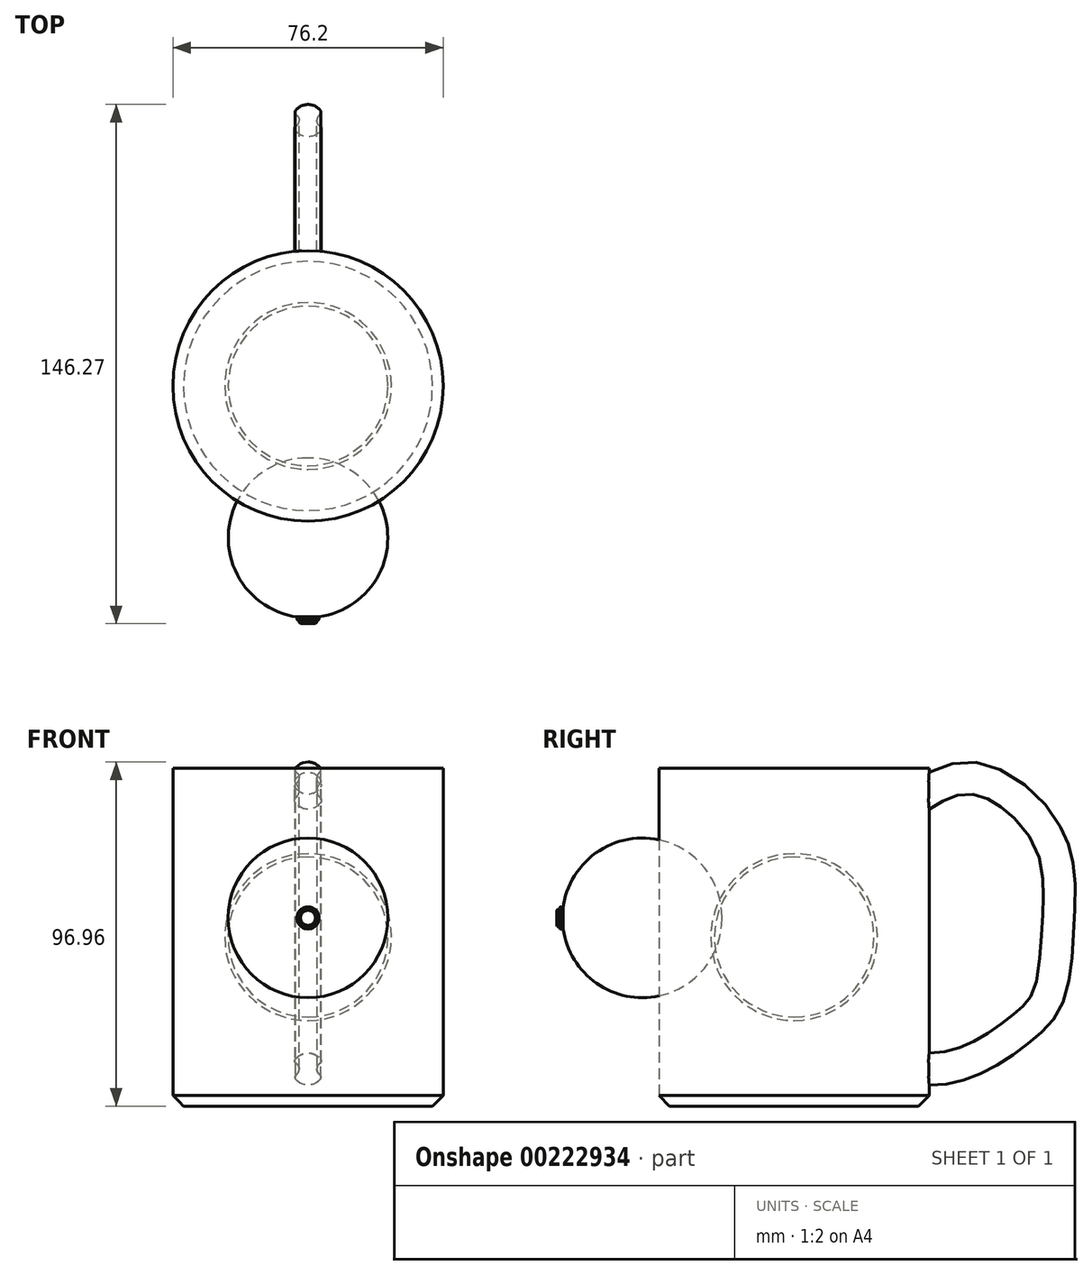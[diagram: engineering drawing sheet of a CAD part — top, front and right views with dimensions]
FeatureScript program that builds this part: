
annotation { "Feature Type Name" : "Feature", "Feature Type Description" : "" }
export const myFeature = defineFeature(function(context is Context, id is Id, definition is map)
    precondition{}
    {
        {
            var Q0;
            Q0=qCreatedBy(makeId("Front.planeOp"),FACE);
            var sketch = newSketch(context, id + "F0", { "sketchPlane" : qUnion([Q0])});
            skLineSegment(sketch, "E0.bottom", {"start": v(0, 0) * mm, "end": v(38.1, 0) * mm});
            skLineSegment(sketch, "E0.top", {"start": v(0, 95.25) * mm, "end": v(38.1, 95.25) * mm});
            skLineSegment(sketch, "E0.left", {"start": v(0, 0) * mm, "end": v(0, 95.25) * mm});
            skLineSegment(sketch, "E0.right", {"start": v(38.1, 0) * mm, "end": v(38.1, 95.25) * mm});
            skSolve(sketch);
        }
        {
            var Q0;
            Q0=makeQuery(id+"F0.imprint","IMPRINT",FACE,{"disambiguationData":[TD([[makeQuery(id+"F0.imprint","IMPRINT",EDGE,{"derivedFrom":sQuery(id+"F0.wireOp",EDGE,"E0.bottom")}),1.0]])]});
            var Q1;
            Q1=sQuery(id+"F0.wireOp",EDGE,"E0.left");
            revolve(context, id + "F1", {"entities" : qUnion([Q0]), "axis" : qUnion([Q1]), "revolveType" : RevolveType.FULL});
        }
        {
            var Q0;
            Q0=makeQuery(id+"F1.opRevolve","SWEPT_FACE",FACE,{"disambiguationData":[OSD([sQuery(id+"F0.wireOp",EDGE,"E0.top")])]});
            var Q1;
            Q1=makeQuery(id+"F1.opRevolve","SWEPT_FACE",FACE,{"disambiguationData":[OSD([sQuery(id+"F0.wireOp",EDGE,"E0.bottom")])]});
            cPlane(context, id + "F2", {"entities" : qUnion([Q0, Q1]), "cplaneType" : CPlaneType.MID_PLANE, "offset" : 25 * mm, "width" : 150 * mm, "height" : 150 * mm});
        }
        {
            var Q0;
            Q0=qCreatedBy(id+"F2.planeOp",FACE);
            var sketch = newSketch(context, id + "F3", { "sketchPlane" : qUnion([Q0])});
            skArc(sketch, "E1", {"start": v(0, -22.5) * mm, "mid": v(22.5, 0) * mm, "end": v(0, 22.5) * mm});
            skArc(sketch, "E2.0", {"start": v(0, -23.5) * mm, "mid": v(23.5, 0) * mm, "end": v(0, 23.5) * mm});
            skLineSegment(sketch, "E3", {"start": v(0, -29.7) * mm, "end": v(0, 30.26) * mm});
            skLineSegment(sketch, "E4.bottom", {"start": v(0, -23.95) * mm, "end": v(4, -23.95) * mm});
            skLineSegment(sketch, "E4.top", {"start": v(0, -22.14) * mm, "end": v(4, -22.14) * mm});
            skLineSegment(sketch, "E4.left", {"start": v(0, -23.95) * mm, "end": v(0, -22.14) * mm});
            skLineSegment(sketch, "E4.right", {"start": v(4, -23.95) * mm, "end": v(4, -22.14) * mm});
            skLineSegment(sketch, "E5.bottom", {"start": v(0, -24.95) * mm, "end": v(2, -24.95) * mm});
            skLineSegment(sketch, "E5.top", {"start": v(0, -22.41) * mm, "end": v(2, -22.41) * mm});
            skLineSegment(sketch, "E5.left", {"start": v(0, -24.95) * mm, "end": v(0, -22.41) * mm});
            skLineSegment(sketch, "E5.right", {"start": v(2, -24.95) * mm, "end": v(2, -23.95) * mm});
            skLineSegment(sketch, "E6", {"start": v(2, -23.95) * mm, "end": v(2, -22.41) * mm});
            skSolve(sketch);
        }
        {
            var Q0;
            {var subQ0=sQuery(id+"F3.wireOp",EDGE,"E1");Q0=makeQuery(id+"F3.imprint","IMPRINT",FACE,{"disambiguationData":[TD([[makeQuery(id+"F3.imprint","IMPRINT",EDGE,{"derivedFrom":subQ0}),1.0]])]});}
            var Q1;
            {var subQ0=sQuery(id+"F3.wireOp",EDGE,"E4.top");Q1=makeQuery(id+"F3.imprint","IMPRINT",FACE,{"disambiguationData":[TD([[makeQuery(id+"F3.imprint","IMPRINT",EDGE,{"derivedFrom":subQ0}),-1.0]])]});}
            var Q2;
            Q2=sQuery(id+"F3.wireOp",EDGE,"E3");
            revolve(context, id + "F4", {"entities" : qUnion([Q0, Q1]), "axis" : qUnion([Q2]), "revolveType" : RevolveType.FULL});
        }
        {
            var Q0;
            {var subQ0=sQuery(id+"F3.wireOp",EDGE,"E1");Q0=makeQuery(id+"F3.imprint","IMPRINT",FACE,{"disambiguationData":[TD([[makeQuery(id+"F3.imprint","IMPRINT",EDGE,{"derivedFrom":subQ0}),-1.0]])]});}
            var Q1;
            Q1=sQuery(id+"F3.wireOp",EDGE,"E3");
            revolve(context, id + "F5", {"entities" : qUnion([Q0]), "axis" : qUnion([Q1]), "revolveType" : RevolveType.FULL});
        }
        {
            var Q0;
            Q0=qCreatedBy(makeId("Front.planeOp"),FACE);
            var sketch = newSketch(context, id + "F6", { "sketchPlane" : qUnion([Q0])});
            skCircle(sketch, "E7", {"center": v(0, 47.62) * mm, "radius": 22.5 * mm});
            skCircle(sketch, "E8", {"center": v(0, 47.62) * mm, "radius": 23.5 * mm});
            skLineSegment(sketch, "E9", {"start": v(0, 47.62) * mm, "end": v(22.5, 47.62) * mm, "construction": true});
            skLineSegment(sketch, "E10", {"start": v(0, 47.62) * mm, "end": v(22.42, 49.54) * mm, "construction": true});
            skLineSegment(sketch, "E11", {"start": v(22.42, 49.54) * mm, "end": v(23.41, 49.62) * mm});
            skLineSegment(sketch, "E12", {"start": v(23.41, 49.62) * mm, "end": v(28.14, 50.03) * mm, "construction": true});
            skLineSegment(sketch, "E13", {"start": v(23.5, 47.62) * mm, "end": v(28.14, 47.62) * mm, "construction": true});
            skLineSegment(sketch, "E14", {"start": v(22.5, 47.62) * mm, "end": v(23.5, 47.62) * mm});
            skLineSegment(sketch, "E15.MirrorCS", {"start": v(22.42, 45.71) * mm, "end": v(23.41, 45.63) * mm});
            skLineSegment(sketch, "E16", {"start": v(0, 47.62) * mm, "end": v(0, 68.38) * mm, "construction": true});
            skSolve(sketch);
        }
        {
            var Q0;
            {var subQ0=sQuery(id+"F6.wireOp",EDGE,"E11");Q0=makeQuery(id+"F6.imprint","IMPRINT",FACE,{"disambiguationData":[TD([[makeQuery(id+"F6.imprint","IMPRINT",EDGE,{"derivedFrom":subQ0}),-1.0]])]});}
            var Q1;
            {var subQ0=sQuery(id+"F6.wireOp",EDGE,"E14");Q1=makeQuery(id+"F6.imprint","IMPRINT",FACE,{"disambiguationData":[TD([[makeQuery(id+"F6.imprint","IMPRINT",EDGE,{"derivedFrom":subQ0}),-1.0]])]});}
            var Q2;
            Q2=sQuery(id+"F6.wireOp",EDGE,"E16");
            revolve(context, id + "F7", {"operationType" : NewBodyOperationType.REMOVE, "entities" : qUnion([Q0, Q1]), "axis" : qUnion([Q2]), "revolveType" : RevolveType.FULL, "oppositeDirection" : true});
        }
        {
            var Q0;
            {var subQ0=sQuery(id+"F3.wireOp",EDGE,"E5.left");var subQ5=sQuery(id+"F3.wireOp",EDGE,"E2.0");var subQ6=makeQuery(id+"F3.imprint","INTERSECT",VERTEX,{"derivedFrom":[subQ5,subQ0]});Q0=makeQuery(id+"F3.imprint","IMPRINT",FACE,{"disambiguationData":[TD([[makeQuery(id+"F3.imprint","IMPRINT",EDGE,{"disambiguationData":[TD([[subQ6,-1.0]])],"derivedFrom":subQ5}),1.0]])]});}
            var Q1;
            {var subQ0=sQuery(id+"F3.wireOp",EDGE,"E4.right");var subQ5=sQuery(id+"F3.wireOp",EDGE,"E2.0");var subQ6=makeQuery(id+"F3.imprint","INTERSECT",VERTEX,{"derivedFrom":[subQ5,subQ0]});Q1=makeQuery(id+"F3.imprint","IMPRINT",FACE,{"disambiguationData":[TD([[makeQuery(id+"F3.imprint","IMPRINT",EDGE,{"disambiguationData":[TD([[subQ6,1.0]])],"derivedFrom":subQ5}),1.0]])]});}
            var Q2;
            Q2=sQuery(id+"F3.wireOp",EDGE,"E4.left");
            revolve(context, id + "F8", {"operationType" : NewBodyOperationType.REMOVE, "entities" : qUnion([Q0, Q1]), "axis" : qUnion([Q2]), "revolveType" : RevolveType.FULL, "oppositeDirection" : true});
        }
        {
            var Q0;
            Q0=qCreatedBy(id+"F2.planeOp",FACE);
            var sketch = newSketch(context, id + "F9", { "sketchPlane" : qUnion([Q0])});
            skArc(sketch, "E17.0.0", {"start": v(3.47, -23.16) * mm, "mid": v(0, 23.41) * mm, "end": v(-3.47, -23.16) * mm, "construction": true});
            skLineSegment(sketch, "E17.0.1", {"start": v(-3.47, -23.16) * mm, "end": v(3.47, -23.16) * mm, "construction": true});
            skLineSegment(sketch, "E18", {"start": v(0, 22.87) * mm, "end": v(0, -24.84) * mm, "construction": true});
            skPoint(sketch, "E18.endSnap0", {"position": v(0, -23.16) * mm});
            skCircle(sketch, "E19", {"center": v(0, 0) * mm, "radius": 22.5 * mm, "construction": true});
            skLineSegment(sketch, "E20.bottom", {"start": v(0, -23.16) * mm, "end": v(3.12, -23.16) * mm});
            skLineSegment(sketch, "E20.top", {"start": v(0, -22.28) * mm, "end": v(3.12, -22.28) * mm});
            skLineSegment(sketch, "E20.left", {"start": v(0, -23.16) * mm, "end": v(0, -22.28) * mm});
            skLineSegment(sketch, "E20.right", {"start": v(3.12, -23.16) * mm, "end": v(3.12, -23.16) * mm});
            skLineSegment(sketch, "E21", {"start": v(3.12, -23.16) * mm, "end": v(3.12, -22.28) * mm});
            skLineSegment(sketch, "E22.bottom", {"start": v(2.62, -23.16) * mm, "end": v(0, -23.16) * mm});
            skLineSegment(sketch, "E22.top", {"start": v(2.62, -24.16) * mm, "end": v(0, -24.16) * mm});
            skLineSegment(sketch, "E22.left", {"start": v(2.62, -23.16) * mm, "end": v(2.62, -24.16) * mm});
            skLineSegment(sketch, "E22.right", {"start": v(0, -23.16) * mm, "end": v(0, -24.16) * mm});
            skSolve(sketch);
        }
        {
            var Q0;
            Q0 = qSketchRegion(id + "F9", true);
            var Q1;
            Q1=sQuery(id+"F9.wireOp",EDGE,"E18");
            revolve(context, id + "F10", {"entities" : qUnion([Q0]), "axis" : qUnion([Q1]), "revolveType" : RevolveType.FULL});
        }
        {
            var Q0;
            Q0=makeQuery(id+"F10.opRevolve","SWEPT_EDGE",EDGE,{"disambiguationData":[OSD([sQuery(id+"F9.wireOp",EDGE,"E22.top"),sQuery(id+"F9.wireOp",EDGE,"E22.left")])]});
            var Q1;
            Q1=makeQuery(id+"F7.boolean.opBoolean","COPY",EDGE,{"derivedFrom":makeQuery(id+"F7.opRevolve","SWEPT_EDGE",EDGE,{"disambiguationData":[OSD([sQuery(id+"F6.wireOp",EDGE,"E8"),sQuery(id+"F6.wireOp",EDGE,"E15.MirrorCS")])]})});
            var Q2;
            Q2=makeQuery(id+"F7.boolean.opBoolean","COPY",EDGE,{"derivedFrom":makeQuery(id+"F7.opRevolve","SWEPT_EDGE",EDGE,{"disambiguationData":[OSD([sQuery(id+"F6.wireOp",EDGE,"E8"),sQuery(id+"F6.wireOp",EDGE,"E11")])]})});
            var Q3;
            {var subQ0=sQuery(id+"F3.wireOp",EDGE,"E2.0");var subQ1=sQuery(id+"F3.wireOp",EDGE,"E4.right");Q3=makeQuery(id+"F8.boolean.opBoolean","COPY",EDGE,{"disambiguationData":[TD([makeQuery(id+"F7.boolean.opBoolean","COPY",FACE,{"derivedFrom":makeQuery(id+"F7.opRevolve","SWEPT_FACE",FACE,{"disambiguationData":[OSD([sQuery(id+"F6.wireOp",EDGE,"E11")])]})})])],"derivedFrom":makeQuery(id+"F8.opRevolve","SWEPT_EDGE",EDGE,{"disambiguationData":[OSD([subQ0,subQ1])]})});}
            var Q4;
            {var subQ0=sQuery(id+"F3.wireOp",EDGE,"E2.0");var subQ1=sQuery(id+"F3.wireOp",EDGE,"E4.right");Q4=makeQuery(id+"F8.boolean.opBoolean","COPY",EDGE,{"disambiguationData":[TD([makeQuery(id+"F7.boolean.opBoolean","COPY",FACE,{"derivedFrom":makeQuery(id+"F7.opRevolve","SWEPT_FACE",FACE,{"disambiguationData":[OSD([sQuery(id+"F6.wireOp",EDGE,"E15.MirrorCS")])]})})])],"derivedFrom":makeQuery(id+"F8.opRevolve","SWEPT_EDGE",EDGE,{"disambiguationData":[OSD([subQ0,subQ1])]})});}
            chamfer(context, id + "F11", {"entities" : qUnion([Q0, Q1, Q2, Q3, Q4]), "width" : .5 * mm, "tangentPropagation" : true});
        }
        {
            var Q0;
            Q0=makeQuery(id+"F10.opRevolve","SWEPT_EDGE",EDGE,{"disambiguationData":[OSD([sQuery(id+"F9.wireOp",EDGE,"E20.bottom"),sQuery(id+"F9.wireOp",EDGE,"E21")])]});
            chamfer(context, id + "F12", {"entities" : qUnion([Q0]), "width" : .1 * mm, "tangentPropagation" : true});
        }
        {
            var Q0;
            Q0=makeQuery(id+"F4.opRevolve","SWEPT_BODY",BODY,{"disambiguationData":[OSD([sQuery(id+"F3.wireOp",EDGE,"E1"),sQuery(id+"F3.wireOp",EDGE,"E3"),sQuery(id+"F3.wireOp",EDGE,"E4.left"),sQuery(id+"F3.wireOp",EDGE,"E5.left")])]});
            var Q1;
            Q1=makeQuery(id+"F7.boolean.opBoolean","SPLIT",BODY,{"disambiguationData":[OD(0.0)],"derivedFrom":makeQuery(id+"F5.opRevolve","SWEPT_BODY",BODY,{"disambiguationData":[OSD([sQuery(id+"F3.wireOp",EDGE,"E1"),sQuery(id+"F3.wireOp",EDGE,"E2.0"),sQuery(id+"F3.wireOp",EDGE,"E3"),sQuery(id+"F3.wireOp",EDGE,"E5.left")])]})});
            var Q2;
            Q2=makeQuery(id+"F7.boolean.opBoolean","SPLIT",BODY,{"disambiguationData":[OD(1.0)],"derivedFrom":makeQuery(id+"F5.opRevolve","SWEPT_BODY",BODY,{"disambiguationData":[OSD([sQuery(id+"F3.wireOp",EDGE,"E1"),sQuery(id+"F3.wireOp",EDGE,"E2.0"),sQuery(id+"F3.wireOp",EDGE,"E3"),sQuery(id+"F3.wireOp",EDGE,"E5.left")])]})});
            var Q3;
            Q3=makeQuery(id+"F10.opRevolve","SWEPT_BODY",BODY,{"disambiguationData":[OSD([sQuery(id+"F9.wireOp",EDGE,"E20.bottom"),sQuery(id+"F9.wireOp",EDGE,"E20.top"),sQuery(id+"F9.wireOp",EDGE,"E20.left"),sQuery(id+"F9.wireOp",EDGE,"E21"),sQuery(id+"F9.wireOp",EDGE,"E22.top"),sQuery(id+"F9.wireOp",EDGE,"E22.left"),sQuery(id+"F9.wireOp",EDGE,"E22.right")])]});
            transform(context, id + "F13", {"entities" : qUnion([Q0, Q1, Q2, Q3]), "transformType" : TransformType.TRANSLATION_3D, "dx" : 0 * mm, "dy" : -42.8 * mm, "dz" : 5.4 * mm, "makeCopy" : false});
        }
        {
            var Q0;
            Q0=qCreatedBy(makeId("Right.planeOp"),FACE);
            var sketch = newSketch(context, id + "F14", { "sketchPlane" : qUnion([Q0])});
            skLineSegment(sketch, "E23.0", {"start": v(38.1, 95.25) * mm, "end": v(-38.1, 95.25) * mm, "construction": true});
            skLineSegment(sketch, "E24", {"start": v(38.1, 95.25) * mm, "end": v(38.1, 0) * mm, "construction": true});
            skLineSegment(sketch, "E25.0", {"start": v(38.1, 0) * mm, "end": v(-38.1, 0) * mm, "construction": true});
            skFitSpline(sketch, "E26", {"points": [v(26.1, 79.7) * mm, v(53.43, 91.8) * mm, v(72.14, 74.66) * mm, v(74.45, 51.46) * mm, v(71.23, 29.88) * mm, v(63.34, 21.36) * mm, v(53.43, 14.53) * mm, v(41.92, 10.62) * mm, v(26.1, 16.09) * mm], "startDerivative": vector(226.9, 201.94) * mm, "endDerivative": vector(-169.73, 138.16) * mm});
            skSolve(sketch);
        }
        {
            var Q0;
            Q0=sQuery(id+"F14.wireOp",EDGE,"E26");
            var Q1;
            Q1=sQuery(id+"F14.wireOp",VERTEX,"E26.0.internal");
            cPlane(context, id + "F15", {"entities" : qUnion([Q0, Q1]), "cplaneType" : CPlaneType.CURVE_POINT, "offset" : 25 * mm, "width" : 150 * mm, "height" : 150 * mm});
        }
        {
            var Q0;
            Q0=qCreatedBy(id+"F15.planeOp",FACE);
            var sketch = newSketch(context, id + "F16", { "sketchPlane" : qUnion([Q0])});
            skArc(sketch, "E27", {"start": v(-3.68, 39.6) * mm, "mid": v(-2.07, 38.2) * mm, "end": v(0, 37.68) * mm});
            skLineSegment(sketch, "E28", {"start": v(0, 42.18) * mm, "end": v(-4.53, 42.18) * mm, "construction": true});
            skArc(sketch, "E29", {"start": v(-3.5, 40.46) * mm, "mid": v(-2.5, 42.03) * mm, "end": v(-3.24, 43.74) * mm});
            skLineSegment(sketch, "E30", {"start": v(0, 37.68) * mm, "end": v(0, 46.19) * mm});
            skArc(sketch, "E31.trimOffspring", {"start": v(0, 46.68) * mm, "mid": v(-1.84, 46.3) * mm, "end": v(-3.36, 45.18) * mm});
            skPoint(sketch, "E32.visualSharp", {"position": v(-4.06, 44.13) * mm});
            skArc(sketch, "E32.filletArc", {"start": v(-3.36, 45.18) * mm, "mid": v(-3.6, 44.43) * mm, "end": v(-3.24, 43.74) * mm});
            skPoint(sketch, "E33.visualSharp", {"position": v(-4.06, 40.23) * mm});
            skArc(sketch, "E33.filletArc", {"start": v(-3.5, 40.46) * mm, "mid": v(-3.78, 40.07) * mm, "end": v(-3.68, 39.6) * mm});
            skArc(sketch, "E34.MirrorCS", {"start": v(0, 46.68) * mm, "mid": v(1.84, 46.3) * mm, "end": v(3.36, 45.18) * mm});
            skArc(sketch, "E35.MirrorCS", {"start": v(3.36, 45.18) * mm, "mid": v(3.6, 44.43) * mm, "end": v(3.24, 43.74) * mm});
            skArc(sketch, "E36.MirrorCS", {"start": v(3.5, 40.46) * mm, "mid": v(2.5, 42.03) * mm, "end": v(3.24, 43.74) * mm});
            skArc(sketch, "E37.MirrorCS", {"start": v(3.5, 40.46) * mm, "mid": v(3.78, 40.07) * mm, "end": v(3.68, 39.6) * mm});
            skArc(sketch, "E38.MirrorCS", {"start": v(3.68, 39.6) * mm, "mid": v(2.07, 38.2) * mm, "end": v(0, 37.68) * mm});
            skSolve(sketch);
        }
        {
            var Q0;
            {var subQ2=sQuery(id+"F16.wireOp",EDGE,"E27");Q0=makeQuery(id+"F16.imprint","IMPRINT",FACE,{"disambiguationData":[TD([[makeQuery(id+"F16.imprint","IMPRINT",EDGE,{"derivedFrom":subQ2}),1.0]])]});}
            var Q1;
            {var subQ0=sQuery(id+"F16.wireOp",EDGE,"E34.MirrorCS");Q1=makeQuery(id+"F16.imprint","IMPRINT",FACE,{"disambiguationData":[TD([[makeQuery(id+"F16.imprint","IMPRINT",EDGE,{"derivedFrom":subQ0}),-1.0]])]});}
            var Q2;
            Q2=sQuery(id+"F14.wireOp",EDGE,"E26");
            sweep(context, id + "F17", {"operationType" : NewBodyOperationType.ADD, "profiles" : qUnion([Q0, Q1]), "path" : qUnion([Q2])});
        }
        {
            var Q0;
            Q0=makeQuery(id+"F1.opRevolve","SWEPT_EDGE",EDGE,{"disambiguationData":[OSD([sQuery(id+"F0.wireOp",EDGE,"E0.bottom"),sQuery(id+"F0.wireOp",EDGE,"E0.right")])]});
            chamfer(context, id + "F18", {"entities" : qUnion([Q0]), "width" : 3 * mm, "tangentPropagation" : true});
        }
    });
